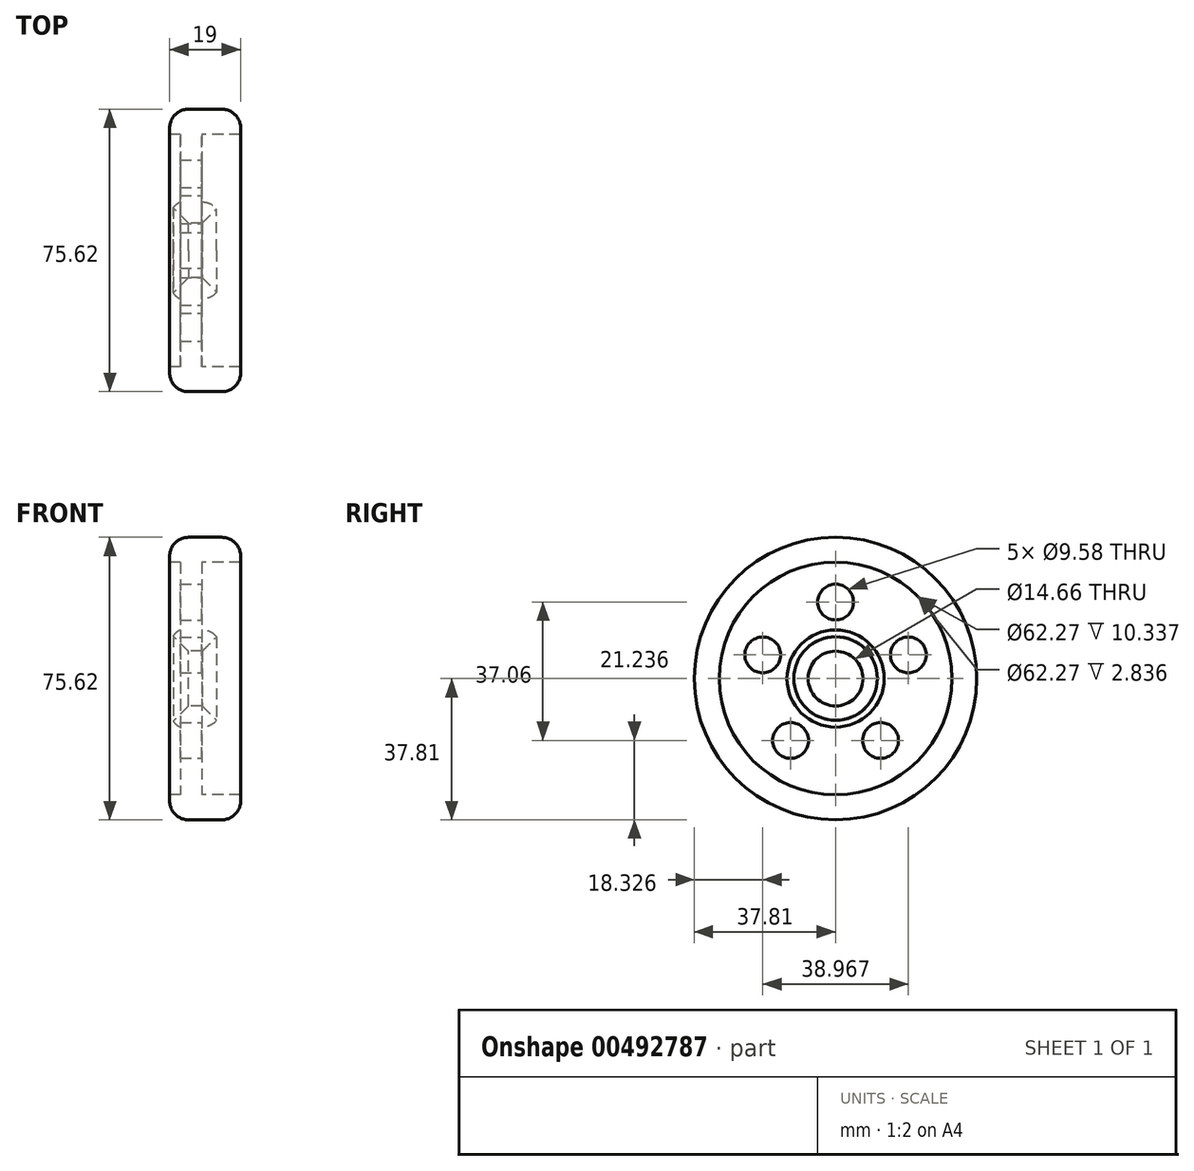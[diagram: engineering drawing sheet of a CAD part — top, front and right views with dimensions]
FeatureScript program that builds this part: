
annotation { "Feature Type Name" : "Feature", "Feature Type Description" : "" }
export const myFeature = defineFeature(function(context is Context, id is Id, definition is map)
    precondition{}
    {
        {
            var Q0;
            Q0=qCreatedBy(makeId("Front.planeOp"),FACE);
            var sketch = newSketch(context, id + "F0", { "sketchPlane" : qUnion([Q0])});
            skLineSegment(sketch, "E0", {"start": v(0, 7.33) * mm, "end": v(13.72, 7.33) * mm});
            skLineSegment(sketch, "E1", {"start": v(13.72, 7.33) * mm, "end": v(13.72, 13) * mm});
            skLineSegment(sketch, "E2", {"start": v(13.72, 13) * mm, "end": v(8.66, 13) * mm});
            skLineSegment(sketch, "E3", {"start": v(8.66, 13) * mm, "end": v(8.66, 31.14) * mm});
            skLineSegment(sketch, "E4", {"start": v(8.66, 31.14) * mm, "end": v(19, 31.14) * mm});
            skLineSegment(sketch, "E5", {"start": v(19, 31.14) * mm, "end": v(19, 37.8) * mm});
            skLineSegment(sketch, "E6", {"start": v(19, 37.8) * mm, "end": v(0, 37.8) * mm});
            skLineSegment(sketch, "E7", {"start": v(0, 37.8) * mm, "end": v(0, 31.14) * mm});
            skLineSegment(sketch, "E8", {"start": v(0, 31.14) * mm, "end": v(2.84, 31.14) * mm});
            skLineSegment(sketch, "E9", {"start": v(2.84, 31.14) * mm, "end": v(2.84, 13) * mm});
            skLineSegment(sketch, "E10", {"start": v(2.84, 13) * mm, "end": v(0, 13) * mm});
            skLineSegment(sketch, "E11", {"start": v(0, 13) * mm, "end": v(0, 7.33) * mm});
            skLineSegment(sketch, "E12", {"start": v(0, 0) * mm, "end": v(13.72, 0) * mm});
            skPoint(sketch, "E12.endSnap0", {"position": v(13.72, 10.16) * mm});
            skSolve(sketch);
        }
        {
            var Q0;
            Q0=makeQuery(id+"F0.imprint","IMPRINT",FACE,{"disambiguationData":[TD([[makeQuery(id+"F0.imprint","IMPRINT",EDGE,{"derivedFrom":sQuery(id+"F0.wireOp",EDGE,"E0")}),1.0]])]});
            var Q1;
            Q1=sQuery(id+"F0.wireOp",EDGE,"E12");
            revolve(context, id + "F1", {"entities" : qUnion([Q0]), "axis" : qUnion([Q1]), "revolveType" : RevolveType.FULL});
        }
        {
            var Q0;
            Q0=makeQuery(id+"F1.opRevolve","SWEPT_FACE",FACE,{"disambiguationData":[OSD([sQuery(id+"F0.wireOp",EDGE,"E3")])]});
            var sketch = newSketch(context, id + "F2", { "sketchPlane" : qUnion([Q0])});
            skCircle(sketch, "E13", {"center": v(0, 20.49) * mm, "radius": 4.8 * mm});
            skCircle(sketch, "E14.1.0", {"center": v(-19.48, 6.33) * mm, "radius": 4.8 * mm});
            skCircle(sketch, "E14.2.0", {"center": v(-12.04, -16.57) * mm, "radius": 4.8 * mm});
            skPoint(sketch, "E14.center", {"position": v(0, 0) * mm});
            skCircle(sketch, "E15.1.3.0", {"center": v(12.04, -16.57) * mm, "radius": 4.8 * mm});
            skCircle(sketch, "E15.1.4.0", {"center": v(19.48, 6.33) * mm, "radius": 4.8 * mm});
            skSolve(sketch);
        }
        {
            var Q0;
            Q0=makeQuery(id+"F2.imprint","IMPRINT",FACE,{"disambiguationData":[TD([[makeQuery(id+"F2.imprint","IMPRINT",EDGE,{"derivedFrom":sQuery(id+"F2.wireOp",EDGE,"E14.1.0")}),1.0]])]});
            var Q1;
            Q1=makeQuery(id+"F2.imprint","IMPRINT",FACE,{"disambiguationData":[TD([[makeQuery(id+"F2.imprint","IMPRINT",EDGE,{"derivedFrom":sQuery(id+"F2.wireOp",EDGE,"E13")}),1.0]])]});
            var Q2;
            Q2=makeQuery(id+"F2.imprint","IMPRINT",FACE,{"disambiguationData":[TD([[makeQuery(id+"F2.imprint","IMPRINT",EDGE,{"derivedFrom":sQuery(id+"F2.wireOp",EDGE,"E15.1.4.0")}),1.0]])]});
            var Q3;
            Q3=makeQuery(id+"F2.imprint","IMPRINT",FACE,{"disambiguationData":[TD([[makeQuery(id+"F2.imprint","IMPRINT",EDGE,{"derivedFrom":sQuery(id+"F2.wireOp",EDGE,"E15.1.3.0")}),1.0]])]});
            var Q4;
            Q4=makeQuery(id+"F2.imprint","IMPRINT",FACE,{"disambiguationData":[TD([[makeQuery(id+"F2.imprint","IMPRINT",EDGE,{"derivedFrom":sQuery(id+"F2.wireOp",EDGE,"E14.2.0")}),1.0]])]});
            extrude(context, id + "F3", {"entities" : qUnion([Q0, Q1, Q2, Q3, Q4]), "operationType" : NewBodyOperationType.REMOVE, "oppositeDirection" : true, "depth" : 25 * mm});
        }
        {
            var Q0;
            Q0=makeQuery(id+"F1.opRevolve","SWEPT_EDGE",EDGE,{"disambiguationData":[OSD([sQuery(id+"F0.wireOp",EDGE,"E6"),sQuery(id+"F0.wireOp",EDGE,"E7")])]});
            var Q1;
            Q1=makeQuery(id+"F1.opRevolve","SWEPT_EDGE",EDGE,{"disambiguationData":[OSD([sQuery(id+"F0.wireOp",EDGE,"E5"),sQuery(id+"F0.wireOp",EDGE,"E6")])]});
            var Q2;
            Q2=makeQuery(id+"F1.opRevolve","SWEPT_EDGE",EDGE,{"disambiguationData":[OSD([sQuery(id+"F0.wireOp",EDGE,"E10"),sQuery(id+"F0.wireOp",EDGE,"E11")])]});
            var Q3;
            Q3=makeQuery(id+"F1.opRevolve","SWEPT_EDGE",EDGE,{"disambiguationData":[OSD([sQuery(id+"F0.wireOp",EDGE,"E1"),sQuery(id+"F0.wireOp",EDGE,"E2")])]});
            fillet(context, id + "F4", {"entities" : qUnion([Q0, Q1, Q2, Q3]), "radius" : 5 * mm, "tangentPropagation" : true, "allowEdgeOverflow" : false});
        }
        {
            var Q0;
            Q0=makeQuery(id+"F1.opRevolve","SWEPT_FACE",FACE,{"disambiguationData":[OSD([sQuery(id+"F0.wireOp",EDGE,"E0")])]});
            chamfer(context, id + "F5", {"entities" : qUnion([Q0]), "width" : 5 * mm, "tangentPropagation" : true});
        }
    });
